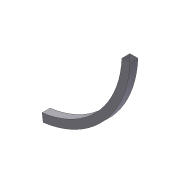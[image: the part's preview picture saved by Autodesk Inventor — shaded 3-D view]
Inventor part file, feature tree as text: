
AUTODESK INVENTOR PART (.ipt)
format: ipt  version: 2012 (Build 160160000, 160)  size: 87,040 bytes
history: native  units: in
note: dims shown in document units (in); Inventor stores cm internally (conversion verified against a paired STEP export)
features: extrude x1, shell x1, sketch x1
ambient origin geometry x8: Origin, YZ Plane, XZ Plane, XY Plane, X Axis, Y Axis, Z Axis, Center Point
bodies: Solid1 (feature_tree)
feature tree (3):
  extrude  "Extrusion1"  Depth=1.0in
  shell  "Shell1"  Thickness=1.0in
  sketch  "Sketch1"  dims[d0=11.5in d1=1.0in d5=1.0in d6=0.0in d7=0.0625in d9=0.5in d10=0.5497in]
